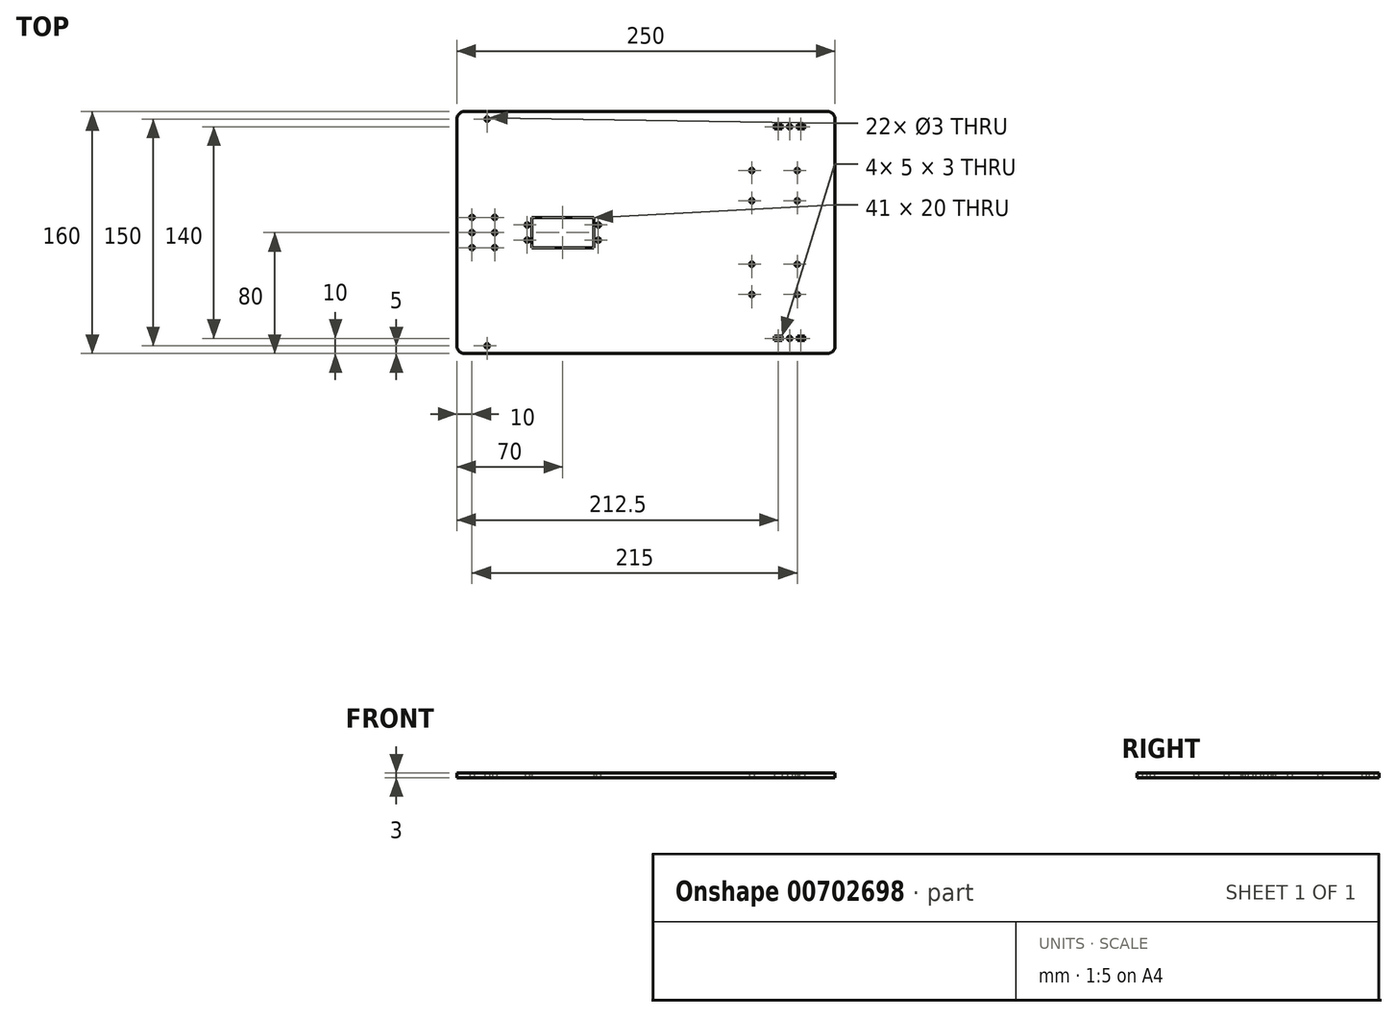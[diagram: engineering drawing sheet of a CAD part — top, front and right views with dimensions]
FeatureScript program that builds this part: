
annotation { "Feature Type Name" : "Feature", "Feature Type Description" : "" }
export const myFeature = defineFeature(function(context is Context, id is Id, definition is map)
    precondition{}
    {
        {
            var Q0;
            Q0=qCreatedBy(makeId("Top.planeOp"),FACE);
            var sketch = newSketch(context, id + "F0", { "sketchPlane" : qUnion([Q0])});
            skLineSegment(sketch, "E0.bottom", {"start": v(5, 160) * mm, "end": v(245, 160) * mm});
            skLineSegment(sketch, "E0.top", {"start": v(5, 0) * mm, "end": v(245, 0) * mm});
            skLineSegment(sketch, "E0.left", {"start": v(0, 155) * mm, "end": v(0, 5) * mm});
            skLineSegment(sketch, "E0.right", {"start": v(250, 155) * mm, "end": v(250, 5) * mm});
            skCircle(sketch, "E1", {"center": v(10, 90) * mm, "radius": 1.5 * mm});
            skCircle(sketch, "E2.1.0.0", {"center": v(20, 155) * mm, "radius": 1.5 * mm});
            skCircle(sketch, "E3.0.1.0", {"center": v(10, 80) * mm, "radius": 1.5 * mm});
            skCircle(sketch, "E3.0.2.0", {"center": v(10, 70) * mm, "radius": 1.5 * mm});
            skLineSegment(sketch, "E3.direction2", {"start": v(10, 90) * mm, "end": v(10, 80) * mm, "construction": true});
            skLineSegment(sketch, "E4", {"start": v(10, 80) * mm, "end": v(0, 80) * mm, "construction": true});
            skLineSegment(sketch, "E5", {"start": v(10, 70) * mm, "end": v(10, 80) * mm, "construction": true});
            skCircle(sketch, "E6.1.0.0", {"center": v(25, 90) * mm, "radius": 1.5 * mm});
            skCircle(sketch, "E6.1.0.1", {"center": v(25, 80) * mm, "radius": 1.5 * mm});
            skCircle(sketch, "E6.1.0.2", {"center": v(25, 70) * mm, "radius": 1.5 * mm});
            skLineSegment(sketch, "E6.direction1", {"start": v(10, 70) * mm, "end": v(25, 70) * mm, "construction": true});
            skLineSegment(sketch, "E7", {"start": v(20, 155) * mm, "end": v(0, 155) * mm, "construction": true});
            skLineSegment(sketch, "E8", {"start": v(20, 155) * mm, "end": v(20, 160) * mm, "construction": true});
            skCircle(sketch, "E9.MirrorC", {"center": v(20, 5) * mm, "radius": 1.5 * mm});
            skCircle(sketch, "E10", {"center": v(46.5, 85) * mm, "radius": 1.5 * mm});
            skCircle(sketch, "E11", {"center": v(46.5, 75) * mm, "radius": 1.5 * mm});
            skLineSegment(sketch, "E12.bottom", {"start": v(49.5, 90) * mm, "end": v(90.5, 90) * mm});
            skLineSegment(sketch, "E12.top", {"start": v(49.5, 70) * mm, "end": v(90.5, 70) * mm});
            skLineSegment(sketch, "E12.left", {"start": v(49.5, 90) * mm, "end": v(49.5, 70) * mm});
            skLineSegment(sketch, "E12.right", {"start": v(90.5, 90) * mm, "end": v(90.5, 70) * mm});
            skPoint(sketch, "E13", {"position": v(60, 80) * mm});
            skCircle(sketch, "E14.MirrorC", {"center": v(93.5, 75) * mm, "radius": 1.5 * mm});
            skCircle(sketch, "E15.MirrorC", {"center": v(93.5, 85) * mm, "radius": 1.5 * mm});
            skCircle(sketch, "E16", {"center": v(220, 150) * mm, "radius": 1.5 * mm});
            skLineSegment(sketch, "E17", {"start": v(220, 150) * mm, "end": v(220, 160) * mm, "construction": true});
            skCircle(sketch, "E18.MirrorC", {"center": v(220, 10) * mm, "radius": 1.5 * mm});
            skPoint(sketch, "E19.visualSharp", {"position": v(0, 160) * mm});
            skArc(sketch, "E19.filletArc", {"start": v(5, 160) * mm, "mid": v(1.46, 158.54) * mm, "end": v(0, 155) * mm});
            skPoint(sketch, "E20.visualSharp", {"position": v(0, 0) * mm});
            skArc(sketch, "E20.filletArc", {"start": v(0, 5) * mm, "mid": v(1.46, 1.46) * mm, "end": v(5, 0) * mm});
            skPoint(sketch, "E21.visualSharp", {"position": v(250, 0) * mm});
            skArc(sketch, "E21.filletArc", {"start": v(245, 0) * mm, "mid": v(248.54, 1.46) * mm, "end": v(250, 5) * mm});
            skPoint(sketch, "E22.visualSharp", {"position": v(250, 160) * mm});
            skArc(sketch, "E22.filletArc", {"start": v(250, 155) * mm, "mid": v(248.54, 158.54) * mm, "end": v(245, 160) * mm});
            skPoint(sketch, "E23.endSnap0", {"position": v(230, 80) * mm});
            skLineSegment(sketch, "E24", {"start": v(250, 80) * mm, "end": v(230, 80) * mm, "construction": true});
            skLineSegment(sketch, "E25.bottom", {"start": v(190, 126) * mm, "end": v(230, 126) * mm, "construction": true});
            skLineSegment(sketch, "E25.top", {"start": v(190, 96) * mm, "end": v(230, 96) * mm, "construction": true});
            skLineSegment(sketch, "E25.left", {"start": v(190, 126) * mm, "end": v(190, 96) * mm, "construction": true});
            skLineSegment(sketch, "E25.right", {"start": v(230, 126) * mm, "end": v(230, 96) * mm, "construction": true});
            skLineSegment(sketch, "E26.bottom", {"start": v(230, 96) * mm, "end": v(190, 96) * mm, "construction": true});
            skLineSegment(sketch, "E26.top", {"start": v(230, 64) * mm, "end": v(190, 64) * mm, "construction": true});
            skLineSegment(sketch, "E26.left", {"start": v(230, 96) * mm, "end": v(230, 64) * mm, "construction": true});
            skLineSegment(sketch, "E26.right", {"start": v(190, 96) * mm, "end": v(190, 64) * mm, "construction": true});
            skLineSegment(sketch, "E27.bottom", {"start": v(190, 64) * mm, "end": v(230, 64) * mm, "construction": true});
            skLineSegment(sketch, "E27.top", {"start": v(190, 34) * mm, "end": v(230, 34) * mm, "construction": true});
            skLineSegment(sketch, "E27.left", {"start": v(190, 64) * mm, "end": v(190, 34) * mm, "construction": true});
            skLineSegment(sketch, "E27.right", {"start": v(230, 64) * mm, "end": v(230, 34) * mm, "construction": true});
            skCircle(sketch, "E28", {"center": v(195, 121) * mm, "radius": 1.5 * mm});
            skLineSegment(sketch, "E29.0", {"start": v(195, 121) * mm, "end": v(225, 121) * mm, "construction": true});
            skLineSegment(sketch, "E29.1", {"start": v(195, 121) * mm, "end": v(195, 101) * mm, "construction": true});
            skLineSegment(sketch, "E29.2", {"start": v(225, 101) * mm, "end": v(195, 101) * mm, "construction": true});
            skLineSegment(sketch, "E29.3", {"start": v(225, 121) * mm, "end": v(225, 101) * mm, "construction": true});
            skLineSegment(sketch, "E30.0", {"start": v(225, 59) * mm, "end": v(195, 59) * mm, "construction": true});
            skLineSegment(sketch, "E30.1", {"start": v(225, 59) * mm, "end": v(225, 39) * mm, "construction": true});
            skLineSegment(sketch, "E30.2", {"start": v(195, 39) * mm, "end": v(225, 39) * mm, "construction": true});
            skLineSegment(sketch, "E30.3", {"start": v(195, 59) * mm, "end": v(195, 39) * mm, "construction": true});
            skCircle(sketch, "E31.1.0.0", {"center": v(225, 121) * mm, "radius": 1.5 * mm});
            skCircle(sketch, "E31.2.0.0", {"center": v(195, 101) * mm, "radius": 1.5 * mm});
            skCircle(sketch, "E31.3.0.0", {"center": v(225, 101) * mm, "radius": 1.5 * mm});
            skCircle(sketch, "E31.4.0.0", {"center": v(195, 59) * mm, "radius": 1.5 * mm});
            skCircle(sketch, "E31.5.0.0", {"center": v(225, 59) * mm, "radius": 1.5 * mm});
            skCircle(sketch, "E31.6.0.0", {"center": v(195, 39) * mm, "radius": 1.5 * mm});
            skCircle(sketch, "E31.7.0.0", {"center": v(225, 39) * mm, "radius": 1.5 * mm});
            skLineSegment(sketch, "E32.bottom", {"start": v(369.13, -180.13) * mm, "end": v(431.13, -180.13) * mm});
            skLineSegment(sketch, "E32.top", {"start": v(369.13, -286.43) * mm, "end": v(431.13, -286.43) * mm});
            skLineSegment(sketch, "E32.left", {"start": v(369.13, -180.13) * mm, "end": v(369.13, -286.43) * mm});
            skLineSegment(sketch, "E32.right", {"start": v(431.13, -180.13) * mm, "end": v(431.13, -286.43) * mm});
            skLineSegment(sketch, "E33.bottom", {"start": v(265.7, -162.51) * mm, "end": v(340.5, -162.51) * mm});
            skLineSegment(sketch, "E33.top", {"start": v(265.7, -215.81) * mm, "end": v(340.5, -215.81) * mm});
            skLineSegment(sketch, "E33.left", {"start": v(265.7, -162.51) * mm, "end": v(265.7, -215.81) * mm});
            skLineSegment(sketch, "E33.right", {"start": v(340.5, -162.51) * mm, "end": v(340.5, -215.81) * mm});
            skLineSegment(sketch, "E34.bottom", {"start": v(253.5, -271.62) * mm, "end": v(363.5, -271.62) * mm});
            skLineSegment(sketch, "E34.top", {"start": v(253.5, -301.62) * mm, "end": v(363.5, -301.62) * mm});
            skLineSegment(sketch, "E34.left", {"start": v(253.5, -271.62) * mm, "end": v(253.5, -301.62) * mm});
            skLineSegment(sketch, "E34.right", {"start": v(363.5, -271.62) * mm, "end": v(363.5, -301.62) * mm});
            skLineSegment(sketch, "E35", {"start": v(225, 11.5) * mm, "end": v(230, 11.5) * mm});
            skLineSegment(sketch, "E36", {"start": v(230, 11.5) * mm, "end": v(230, 8.5) * mm});
            skLineSegment(sketch, "E37", {"start": v(230, 8.5) * mm, "end": v(225, 8.5) * mm});
            skLineSegment(sketch, "E38", {"start": v(225, 8.5) * mm, "end": v(225, 11.5) * mm});
            skPoint(sketch, "E39", {"position": v(225, 10) * mm});
            skLineSegment(sketch, "E40.MirrorCS", {"start": v(210, 8.5) * mm, "end": v(215, 8.5) * mm});
            skLineSegment(sketch, "E41.MirrorCS", {"start": v(210, 11.5) * mm, "end": v(210, 8.5) * mm});
            skLineSegment(sketch, "E42.MirrorCS", {"start": v(215, 11.5) * mm, "end": v(210, 11.5) * mm});
            skLineSegment(sketch, "E43.MirrorCS", {"start": v(215, 8.5) * mm, "end": v(215, 11.5) * mm});
            skLineSegment(sketch, "E44.MirrorCS", {"start": v(225, 151.5) * mm, "end": v(225, 148.5) * mm});
            skLineSegment(sketch, "E45.MirrorCS", {"start": v(230, 151.5) * mm, "end": v(225, 151.5) * mm});
            skLineSegment(sketch, "E46.MirrorCS", {"start": v(225, 148.5) * mm, "end": v(230, 148.5) * mm});
            skLineSegment(sketch, "E47.MirrorCS", {"start": v(215, 148.5) * mm, "end": v(210, 148.5) * mm});
            skLineSegment(sketch, "E48.MirrorCS", {"start": v(215, 151.5) * mm, "end": v(215, 148.5) * mm});
            skLineSegment(sketch, "E49.MirrorCS", {"start": v(210, 148.5) * mm, "end": v(210, 151.5) * mm});
            skPoint(sketch, "E50.MirrorP", {"position": v(225, 150) * mm});
            skLineSegment(sketch, "E51.MirrorCS", {"start": v(230, 148.5) * mm, "end": v(230, 151.5) * mm});
            skLineSegment(sketch, "E52.MirrorCS", {"start": v(210, 151.5) * mm, "end": v(215, 151.5) * mm});
            skLineSegment(sketch, "E53", {"start": v(10, 80) * mm, "end": v(49.5, 80) * mm, "construction": true});
            skPoint(sketch, "E54", {"position": v(49.5, 80) * mm});
            skLineSegment(sketch, "E55", {"start": v(215, 10) * mm, "end": v(220, 10) * mm, "construction": true});
            skLineSegment(sketch, "E56", {"start": v(220, 10) * mm, "end": v(225, 10) * mm, "construction": true});
            skLineSegment(sketch, "E57.1.0.0", {"start": v(480, -216.42) * mm, "end": v(440, -216.42) * mm, "construction": true});
            skPoint(sketch, "E57.1.0.3", {"position": v(500, -312.42) * mm});
            skPoint(sketch, "E57.1.0.5", {"position": v(250, -312.42) * mm});
            skLineSegment(sketch, "E57.1.0.6", {"start": v(255, -152.42) * mm, "end": v(495, -152.42) * mm});
            skPoint(sketch, "E57.1.0.7", {"position": v(250, -152.42) * mm});
            skLineSegment(sketch, "E57.1.0.8", {"start": v(255, -312.42) * mm, "end": v(495, -312.42) * mm});
            skLineSegment(sketch, "E57.1.0.9", {"start": v(250, -157.42) * mm, "end": v(250, -307.42) * mm});
            skLineSegment(sketch, "E57.1.0.10", {"start": v(500, -157.42) * mm, "end": v(500, -307.42) * mm});
            skPoint(sketch, "E57.1.0.11", {"position": v(500, -152.42) * mm});
            skLineSegment(sketch, "E57.1.0.12", {"start": v(299.5, -242.42) * mm, "end": v(340.5, -242.42) * mm});
            skPoint(sketch, "E57.1.0.13", {"position": v(299.5, -232.42) * mm});
            skPoint(sketch, "E57.1.0.14", {"position": v(310, -232.42) * mm});
            skLineSegment(sketch, "E57.1.0.15", {"start": v(440, -186.42) * mm, "end": v(480, -186.42) * mm, "construction": true});
            skLineSegment(sketch, "E57.1.0.16", {"start": v(299.5, -222.42) * mm, "end": v(340.5, -222.42) * mm});
            skLineSegment(sketch, "E57.1.0.18", {"start": v(440, -248.42) * mm, "end": v(480, -248.42) * mm, "construction": true});
            skPoint(sketch, "E57.1.0.19", {"position": v(475, -302.42) * mm});
            skPoint(sketch, "E57.1.0.20", {"position": v(475, -162.42) * mm});
            skLineSegment(sketch, "E57.1.0.22", {"start": v(440, -278.42) * mm, "end": v(480, -278.42) * mm, "construction": true});
            skCircle(sketch, "E57.1.0.24", {"center": v(275, -222.42) * mm, "radius": 1.5 * mm});
            skLineSegment(sketch, "E57.1.0.25", {"start": v(440, -216.42) * mm, "end": v(480, -216.42) * mm, "construction": true});
            skCircle(sketch, "E57.1.0.27", {"center": v(270, -307.42) * mm, "radius": 1.5 * mm});
            skLineSegment(sketch, "E57.1.0.29", {"start": v(480, -248.42) * mm, "end": v(440, -248.42) * mm, "construction": true});
            skCircle(sketch, "E57.1.0.32", {"center": v(275, -232.42) * mm, "radius": 1.5 * mm});
            skPoint(sketch, "E57.1.0.33", {"position": v(299.5, -232.42) * mm});
            skLineSegment(sketch, "E57.1.0.34", {"start": v(480, -186.42) * mm, "end": v(480, -216.42) * mm, "construction": true});
            skLineSegment(sketch, "E57.1.0.35", {"start": v(299.5, -222.42) * mm, "end": v(299.5, -242.42) * mm});
            skLineSegment(sketch, "E57.1.0.36", {"start": v(460, -163.92) * mm, "end": v(460, -160.92) * mm});
            skCircle(sketch, "E57.1.0.37", {"center": v(475, -191.42) * mm, "radius": 1.5 * mm});
            skCircle(sketch, "E57.1.0.38", {"center": v(343.5, -227.42) * mm, "radius": 1.5 * mm});
            skLineSegment(sketch, "E57.1.0.42", {"start": v(440, -186.42) * mm, "end": v(440, -216.42) * mm, "construction": true});
            skLineSegment(sketch, "E57.1.0.43", {"start": v(340.5, -222.42) * mm, "end": v(340.5, -242.42) * mm});
            skCircle(sketch, "E57.1.0.44", {"center": v(343.5, -237.42) * mm, "radius": 1.5 * mm});
            skCircle(sketch, "E57.1.0.45", {"center": v(445, -273.42) * mm, "radius": 1.5 * mm});
            skLineSegment(sketch, "E57.1.0.46", {"start": v(440, -248.42) * mm, "end": v(440, -278.42) * mm, "construction": true});
            skArc(sketch, "E57.1.0.47", {"start": v(250, -307.42) * mm, "mid": v(251.46, -310.96) * mm, "end": v(255, -312.42) * mm});
            skArc(sketch, "E57.1.0.48", {"start": v(495, -312.42) * mm, "mid": v(498.54, -310.96) * mm, "end": v(500, -307.42) * mm});
            skCircle(sketch, "E57.1.0.49", {"center": v(275, -242.42) * mm, "radius": 1.5 * mm});
            skCircle(sketch, "E57.1.0.51", {"center": v(260, -222.42) * mm, "radius": 1.5 * mm});
            skCircle(sketch, "E57.1.0.52", {"center": v(260, -242.42) * mm, "radius": 1.5 * mm});
            skCircle(sketch, "E57.1.0.54", {"center": v(475, -273.42) * mm, "radius": 1.5 * mm});
            skLineSegment(sketch, "E57.1.0.55", {"start": v(480, -248.42) * mm, "end": v(480, -278.42) * mm, "construction": true});
            skArc(sketch, "E57.1.0.56", {"start": v(500, -157.42) * mm, "mid": v(498.54, -153.88) * mm, "end": v(495, -152.42) * mm});
            skLineSegment(sketch, "E57.1.0.58", {"start": v(465, -163.92) * mm, "end": v(460, -163.92) * mm});
            skLineSegment(sketch, "E57.1.0.59", {"start": v(480, -163.92) * mm, "end": v(480, -160.92) * mm});
            skCircle(sketch, "E57.1.0.60", {"center": v(445, -211.42) * mm, "radius": 1.5 * mm});
            skCircle(sketch, "E57.1.0.61", {"center": v(475, -211.42) * mm, "radius": 1.5 * mm});
            skLineSegment(sketch, "E57.1.0.62", {"start": v(460, -160.92) * mm, "end": v(465, -160.92) * mm});
            skCircle(sketch, "E57.1.0.63", {"center": v(296.5, -227.42) * mm, "radius": 1.5 * mm});
            skLineSegment(sketch, "E57.1.0.64", {"start": v(475, -163.92) * mm, "end": v(480, -163.92) * mm});
            skCircle(sketch, "E57.1.0.65", {"center": v(445, -253.42) * mm, "radius": 1.5 * mm});
            skCircle(sketch, "E57.1.0.66", {"center": v(470, -162.42) * mm, "radius": 1.5 * mm});
            skCircle(sketch, "E57.1.0.67", {"center": v(445, -191.42) * mm, "radius": 1.5 * mm});
            skCircle(sketch, "E57.1.0.69", {"center": v(270, -157.42) * mm, "radius": 1.5 * mm});
            skLineSegment(sketch, "E57.1.0.71", {"start": v(480, -160.92) * mm, "end": v(475, -160.92) * mm});
            skCircle(sketch, "E57.1.0.72", {"center": v(296.5, -237.42) * mm, "radius": 1.5 * mm});
            skLineSegment(sketch, "E57.1.0.74", {"start": v(475, -160.92) * mm, "end": v(475, -163.92) * mm});
            skLineSegment(sketch, "E57.1.0.75", {"start": v(465, -160.92) * mm, "end": v(465, -163.92) * mm});
            skCircle(sketch, "E57.1.0.76", {"center": v(475, -253.42) * mm, "radius": 1.5 * mm});
            skCircle(sketch, "E57.1.0.77", {"center": v(260, -232.42) * mm, "radius": 1.5 * mm});
            skArc(sketch, "E57.1.0.79", {"start": v(255, -152.42) * mm, "mid": v(251.46, -153.88) * mm, "end": v(250, -157.42) * mm});
            skLineSegment(sketch, "E57.1.0.80", {"start": v(465, -303.92) * mm, "end": v(465, -300.92) * mm});
            skCircle(sketch, "E57.1.0.81", {"center": v(470, -302.42) * mm, "radius": 1.5 * mm});
            skLineSegment(sketch, "E57.1.0.82", {"start": v(470, -302.42) * mm, "end": v(475, -302.42) * mm, "construction": true});
            skLineSegment(sketch, "E57.1.0.83", {"start": v(480, -303.92) * mm, "end": v(475, -303.92) * mm});
            skLineSegment(sketch, "E57.1.0.84", {"start": v(475, -300.92) * mm, "end": v(480, -300.92) * mm});
            skLineSegment(sketch, "E57.1.0.85", {"start": v(460, -300.92) * mm, "end": v(460, -303.92) * mm});
            skLineSegment(sketch, "E57.1.0.86", {"start": v(465, -302.42) * mm, "end": v(470, -302.42) * mm, "construction": true});
            skLineSegment(sketch, "E57.1.0.87", {"start": v(465, -300.92) * mm, "end": v(460, -300.92) * mm});
            skLineSegment(sketch, "E57.1.0.88", {"start": v(460, -303.92) * mm, "end": v(465, -303.92) * mm});
            skLineSegment(sketch, "E57.1.0.89", {"start": v(480, -300.92) * mm, "end": v(480, -303.92) * mm});
            skLineSegment(sketch, "E57.1.0.90", {"start": v(475, -303.92) * mm, "end": v(475, -300.92) * mm});
            skText(sketch, "E58", { "text": "Arduino", "fontName": "Arimo-Regular.ttf"});
            skText(sketch, "E59", { "text": "Battery", "fontName": "OpenSans-Regular.ttf"});
            skText(sketch, "E60", { "text": "Driver", "fontName": "OpenSans-Regular.ttf"});
            skText(sketch, "E61", { "text": "Duct", "fontName": "OpenSans-Regular.ttf"});
            skText(sketch, "E62", { "text": "servo", "fontName": "OpenSans-Regular.ttf"});
            const initialGuessF0  = {"E58": [0.27552, -0.19493, 1, 0, 0.01036], "E59": [0.27513, -0.29306, 1, 0, 0.0133], "E60": [0.40541, -0.25952, 0, 1, 0.01237], "E61": [0.46872, -0.26334, 0, 1, 0.0195], "E62": [0.30582, -0.23628, 1, 0, 0.00718]};
            skSetInitialGuess(sketch, initialGuessF0);
            skSolve(sketch);
        }
        {
            var Q0;
            Q0=makeQuery(id+"F0.imprint","IMPRINT",FACE,{"disambiguationData":[TD([[makeQuery(id+"F0.imprint","IMPRINT",EDGE,{"derivedFrom":sQuery(id+"F0.wireOp",EDGE,"E0.bottom")}),-1.0]])]});
            extrude(context, id + "F1", {"entities" : qUnion([Q0]), "depth" : 3 * mm, "offsetDistance" : 25.4 * mm});
        }
    });
